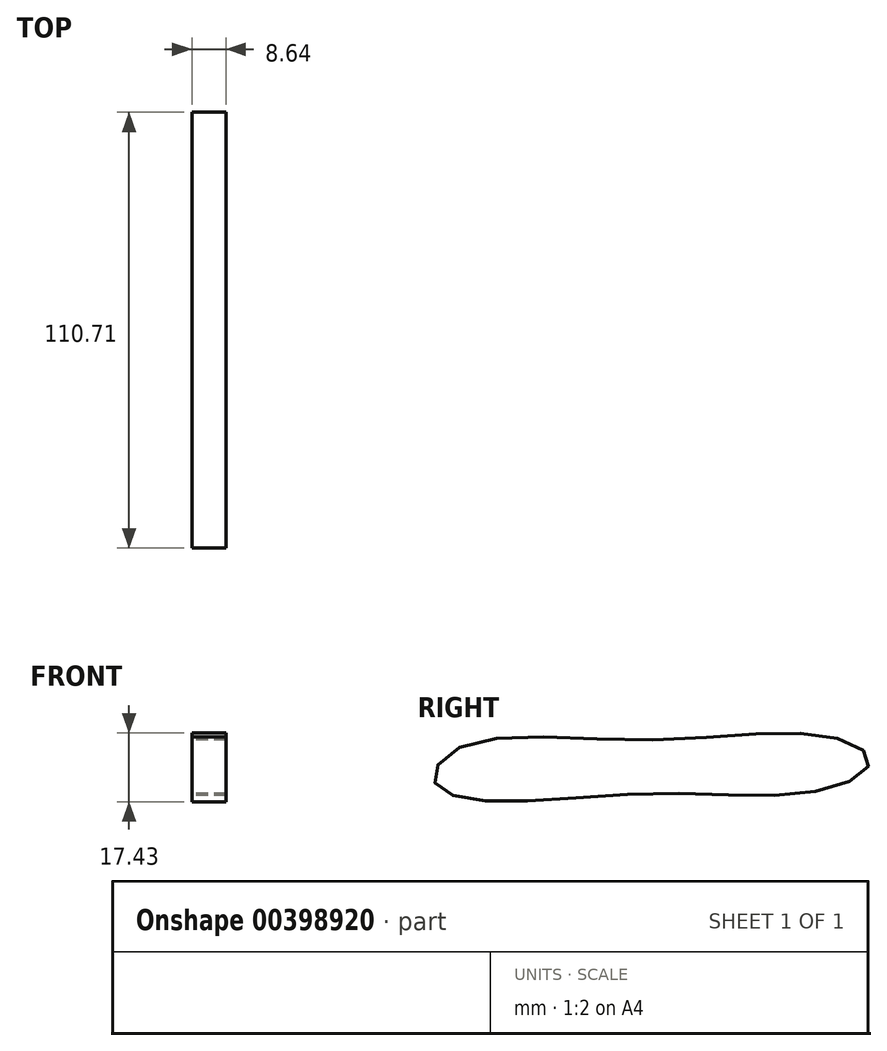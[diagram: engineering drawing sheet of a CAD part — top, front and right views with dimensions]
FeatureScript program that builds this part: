
annotation { "Feature Type Name" : "Feature", "Feature Type Description" : "" }
export const myFeature = defineFeature(function(context is Context, id is Id, definition is map)
    precondition{}
    {
        {
            var Q0;
            Q0=qCreatedBy(makeId("Right.planeOp"),FACE);
            var sketch = newSketch(context, id + "F0", { "sketchPlane" : qUnion([Q0])});
            skFitSpline(sketch, "E0", {"points": [v(0, 10.1) * mm, v(45.06, 10.93) * mm, v(55.09, 4.52) * mm, v(43.1, -2.72) * mm, v(0, -3.56) * mm, v(-45.24, -5.23) * mm, v(-55.55, 0) * mm, v(-48.3, 8.42) * mm, v(0, 10.1) * mm]});
            skSolve(sketch);
        }
        {
            var Q0;
            Q0=makeQuery(id+"F0.imprint","IMPRINT",FACE,{"disambiguationData":[TD([[makeQuery(id+"F0.imprint","IMPRINT",EDGE,{"derivedFrom":sQuery(id+"F0.wireOp",EDGE,"E0")}),-1.0]])]});
            extrude(context, id + "F1", {"entities" : qUnion([Q0]), "depth" : 8.64 * mm});
        }
    });
